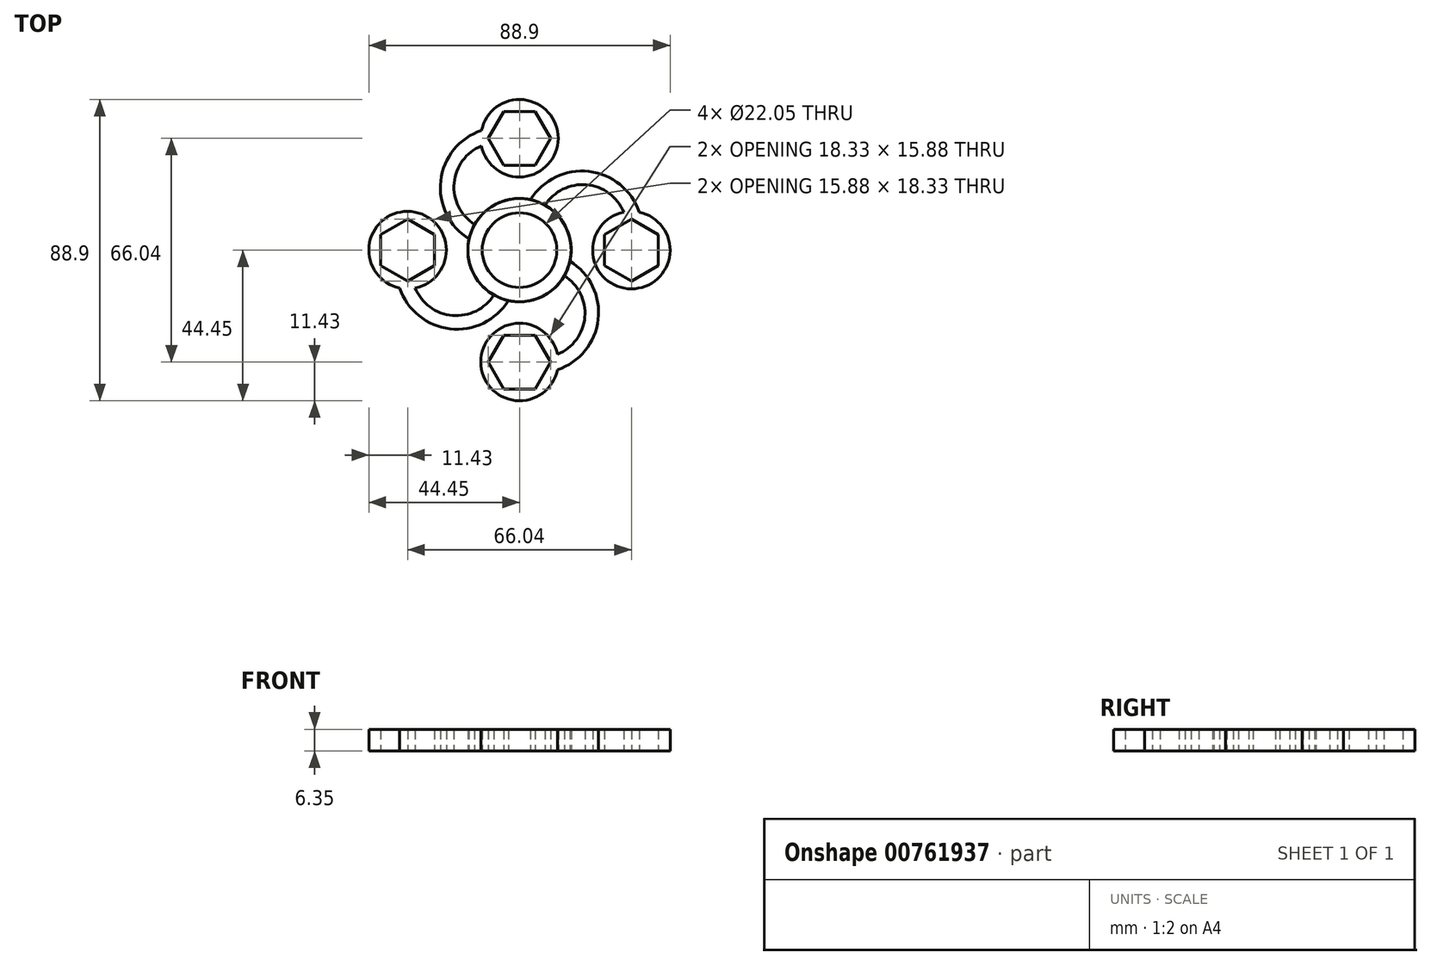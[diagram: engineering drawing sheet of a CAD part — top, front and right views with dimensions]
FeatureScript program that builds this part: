
annotation { "Feature Type Name" : "Feature", "Feature Type Description" : "" }
export const myFeature = defineFeature(function(context is Context, id is Id, definition is map)
    precondition{}
    {
        {
            var Q0;
            Q0=qCreatedBy(makeId("Top.planeOp"),FACE);
            var sketch = newSketch(context, id + "F0", { "sketchPlane" : qUnion([Q0])});
            skCircle(sketch, "E0", {"center": v(0, 0) * mm, "radius": 15.24 * mm});
            skCircle(sketch, "E1", {"center": v(0, 0) * mm, "radius": 11.02 * mm});
            skCircle(sketch, "E2", {"center": v(0, 33.02) * mm, "radius": 11.43 * mm});
            skCircle(sketch, "E3.cCircle", {"center": v(0, 33.02) * mm, "radius": 7.94 * mm, "construction": true});
            skLineSegment(sketch, "E3.0", {"start": v(4.58, 25.08) * mm, "end": v(-4.58, 25.08) * mm});
            skLineSegment(sketch, "E3.1", {"start": v(-4.58, 25.08) * mm, "end": v(-9.17, 33.02) * mm});
            skLineSegment(sketch, "E3.2", {"start": v(-9.17, 33.02) * mm, "end": v(-4.58, 40.96) * mm});
            skLineSegment(sketch, "E3.3", {"start": v(-4.58, 40.96) * mm, "end": v(4.58, 40.96) * mm});
            skLineSegment(sketch, "E3.4", {"start": v(4.58, 40.96) * mm, "end": v(9.17, 33.02) * mm});
            skLineSegment(sketch, "E3.5", {"start": v(9.17, 33.02) * mm, "end": v(4.58, 25.08) * mm});
            skPoint(sketch, "E3.0.midPoint", {"position": v(0, 25.08) * mm});
            skArc(sketch, "E4", {"start": v(-11.2, 30.76) * mm, "mid": v(-19.29, 19.77) * mm, "end": v(-13.24, 7.55) * mm});
            skArc(sketch, "E5", {"start": v(-11.2, 35.33) * mm, "mid": v(-23.22, 20.48) * mm, "end": v(-14.88, 3.29) * mm});
            skArc(sketch, "E6.MirrorCS", {"start": v(11.2, 35.33) * mm, "mid": v(23.22, 20.48) * mm, "end": v(14.88, 3.29) * mm});
            skArc(sketch, "E7.MirrorCS", {"start": v(11.2, 30.76) * mm, "mid": v(19.29, 19.77) * mm, "end": v(13.24, 7.55) * mm});
            skSolve(sketch);
        }
        {
            var Q0;
            Q0=makeQuery(id+"F0.imprint","IMPRINT",FACE,{"disambiguationData":[TD([[makeQuery(id+"F0.imprint","IMPRINT",EDGE,{"derivedFrom":sQuery(id+"F0.wireOp",EDGE,"E3.0")}),1.0]])]});
            var Q1;
            {var subQ0=sQuery(id+"F0.wireOp",EDGE,"E4");Q1=makeQuery(id+"F0.imprint","IMPRINT",FACE,{"disambiguationData":[TD([[makeQuery(id+"F0.imprint","IMPRINT",EDGE,{"derivedFrom":subQ0}),-1.0]])]});}
            var Q2;
            Q2=makeQuery(id+"F0.imprint","IMPRINT",FACE,{"disambiguationData":[TD([[makeQuery(id+"F0.imprint","IMPRINT",EDGE,{"derivedFrom":sQuery(id+"F0.wireOp",EDGE,"E1")}),-1.0]])]});
            var Q3;
            {var subQ0=sQuery(id+"F0.wireOp",EDGE,"E6.MirrorCS");Q3=makeQuery(id+"F0.imprint","IMPRINT",FACE,{"disambiguationData":[TD([[makeQuery(id+"F0.imprint","IMPRINT",EDGE,{"derivedFrom":subQ0}),-1.0]])]});}
            extrude(context, id + "F1", {"entities" : qUnion([Q0, Q1, Q2, Q3]), "depth" : 6.35 * mm, "offsetDistance" : 25.4 * mm});
        }
        {
            var Q0;
            Q0=makeQuery(id+"F1.opExtrude","SWEPT_BODY",BODY,{"disambiguationData":[OSD([sQuery(id+"F0.wireOp",EDGE,"E0"),sQuery(id+"F0.wireOp",EDGE,"E1"),sQuery(id+"F0.wireOp",EDGE,"E2"),sQuery(id+"F0.wireOp",EDGE,"E3.0"),sQuery(id+"F0.wireOp",EDGE,"E3.1"),sQuery(id+"F0.wireOp",EDGE,"E3.2"),sQuery(id+"F0.wireOp",EDGE,"E3.3"),sQuery(id+"F0.wireOp",EDGE,"E3.4"),sQuery(id+"F0.wireOp",EDGE,"E3.5"),sQuery(id+"F0.wireOp",EDGE,"E4"),sQuery(id+"F0.wireOp",EDGE,"E5"),sQuery(id+"F0.wireOp",EDGE,"E6.MirrorCS"),sQuery(id+"F0.wireOp",EDGE,"E7.MirrorCS")])]});
            var Q1;
            Q1=makeQuery(id+"F1.opExtrude","CAP_EDGE",EDGE,{"disambiguationData":[OSD([sQuery(id+"F0.wireOp",EDGE,"E1")])],"isStart":false});
            circularPattern(context, id + "F2", {"entities" : qUnion([Q0]), "axis" : qUnion([Q1]), "angle" : 360 * degree, "instanceCount" : 4, "equalSpace" : true});
        }
    });
